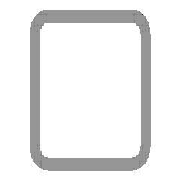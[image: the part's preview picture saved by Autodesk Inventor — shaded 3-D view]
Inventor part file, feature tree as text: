
AUTODESK INVENTOR PART (.ipt)
format: ipt  version: 2025 (Build 290162010, 162A)  size: 134,144 bytes
history: native  units: mm (DEFAULTED — no unit token found)
features: other x4, sketch x1, plane x1
ambient origin geometry x8: Origin, YZ Plane, XZ Plane, XY Plane, X Axis, Y Axis, Z Axis, Center Point
bodies: Solid1 (feature_tree), Body (feature_tree)
feature tree (6):
  parser-record x1  (decoder bookkeeping rows leaked as tree rows — omitted from the tree; the rows remain in map.json)
  other  "Driven Length"
  other  "Start Plane"
  other  "End Plane"
  sketch  "Sketch3"  dims[d3=3000.0mm d4=0.0mm d7=6.0mm d9=100.0mm d11=100.0mm d12=3.0mm d13=-0.0mm d14=3000.0mm d15=50.0mm d16=50.0mm d17=90.0deg d18=3000.0mm]
  plane  "Work Plane3"
